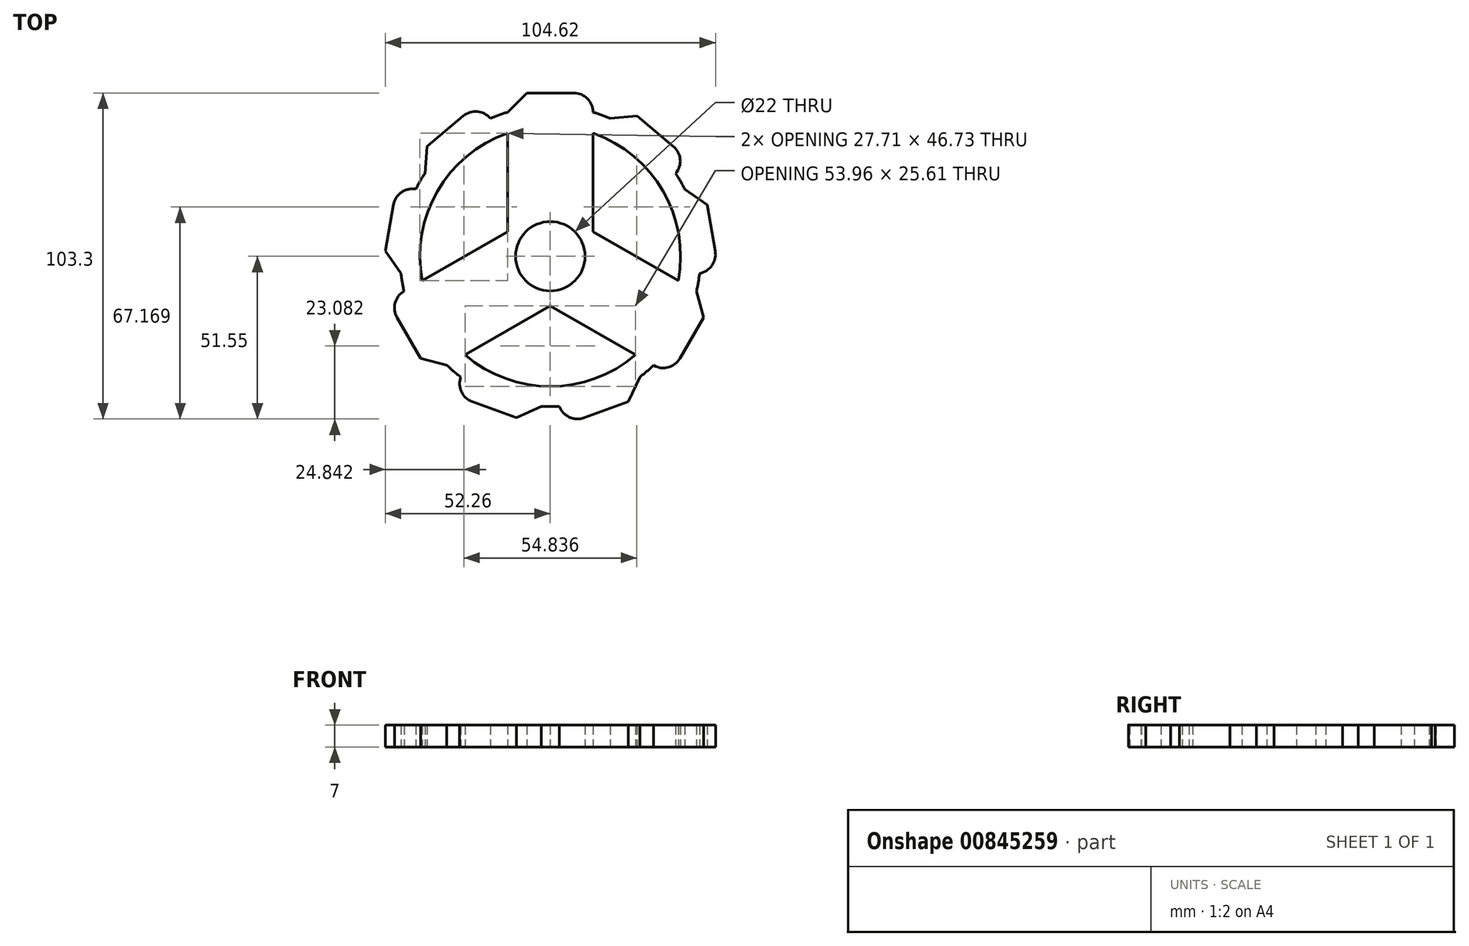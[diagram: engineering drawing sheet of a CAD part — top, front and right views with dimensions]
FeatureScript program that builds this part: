
annotation { "Feature Type Name" : "Feature", "Feature Type Description" : "" }
export const myFeature = defineFeature(function(context is Context, id is Id, definition is map)
    precondition{}
    {
        {
            var Q0;
            Q0=qCreatedBy(makeId("Top.planeOp"),FACE);
            var sketch = newSketch(context, id + "F0", { "sketchPlane" : qUnion([Q0])});
            skCircle(sketch, "E0", {"center": v(0, 0) * mm, "radius": 11 * mm});
            skCircle(sketch, "E1", {"center": v(0, 0) * mm, "radius": 13.56 * mm});
            skArc(sketch, "E2", {"start": v(-13.56, 38.98) * mm, "mid": v(0, -41.28) * mm, "end": v(13.56, 38.98) * mm});
            skArc(sketch, "E3", {"start": v(-13.56, 45.65) * mm, "mid": v(-16.29, 44.75) * mm, "end": v(-18.95, 43.7) * mm});
            skLineSegment(sketch, "E4.left", {"start": v(-13.56, 7.83) * mm, "end": v(-13.56, 38.98) * mm});
            skLineSegment(sketch, "E4.right", {"start": v(13.56, 7.83) * mm, "end": v(13.56, 38.98) * mm});
            skPoint(sketch, "E5.orphan", {"position": v(-13.56, 0) * mm});
            skLineSegment(sketch, "E6.top", {"start": v(-7.46, 51.75) * mm, "end": v(7.46, 51.75) * mm});
            skLineSegment(sketch, "E6.left", {"start": v(-13.56, 38.98) * mm, "end": v(-13.56, 45.65) * mm, "construction": true});
            skLineSegment(sketch, "E6.right", {"start": v(13.56, 38.98) * mm, "end": v(13.56, 45.65) * mm, "construction": true});
            skArc(sketch, "E7.filletArc", {"start": v(13.56, 45.65) * mm, "mid": v(11.78, 49.97) * mm, "end": v(7.46, 51.75) * mm});
            skLineSegment(sketch, "E8", {"start": v(-13.56, 45.65) * mm, "end": v(-7.46, 51.75) * mm});
            skLineSegment(sketch, "E9.1.0", {"start": v(-41.09, -32.34) * mm, "end": v(-48.55, -19.41) * mm});
            skLineSegment(sketch, "E9.1.1", {"start": v(-32.75, -34.57) * mm, "end": v(-41.09, -32.34) * mm});
            skLineSegment(sketch, "E9.1.2", {"start": v(-26.98, -31.24) * mm, "end": v(-32.75, -34.57) * mm, "construction": true});
            skLineSegment(sketch, "E9.1.3", {"start": v(0, -15.66) * mm, "end": v(-26.98, -31.24) * mm});
            skLineSegment(sketch, "E9.1.4", {"start": v(-13.56, 7.83) * mm, "end": v(-40.54, -7.74) * mm});
            skLineSegment(sketch, "E9.1.5", {"start": v(-40.54, -7.74) * mm, "end": v(-46.32, -11.08) * mm, "construction": true});
            skArc(sketch, "E9.1.6", {"start": v(-46.32, -11.08) * mm, "mid": v(-49.16, -14.78) * mm, "end": v(-48.55, -19.41) * mm});
            skLineSegment(sketch, "E9.2.0", {"start": v(48.55, -19.41) * mm, "end": v(41.09, -32.34) * mm});
            skLineSegment(sketch, "E9.2.1", {"start": v(46.32, -11.08) * mm, "end": v(48.55, -19.41) * mm});
            skLineSegment(sketch, "E9.2.2", {"start": v(40.54, -7.74) * mm, "end": v(46.32, -11.08) * mm, "construction": true});
            skLineSegment(sketch, "E9.2.3", {"start": v(13.56, 7.83) * mm, "end": v(40.54, -7.74) * mm});
            skLineSegment(sketch, "E9.2.4", {"start": v(0, -15.66) * mm, "end": v(26.98, -31.24) * mm});
            skLineSegment(sketch, "E9.2.5", {"start": v(26.98, -31.24) * mm, "end": v(32.75, -34.57) * mm, "construction": true});
            skArc(sketch, "E9.2.6", {"start": v(32.75, -34.57) * mm, "mid": v(37.38, -35.18) * mm, "end": v(41.09, -32.34) * mm});
            skPoint(sketch, "E10.orphan", {"position": v(-6.78, 11.75) * mm});
            skPoint(sketch, "E11.orphan", {"position": v(6.78, 11.75) * mm});
            skPoint(sketch, "E12.orphan", {"position": v(13.56, 0) * mm});
            skPoint(sketch, "E13.orphan", {"position": v(6.78, -11.75) * mm});
            skPoint(sketch, "E14.orphan", {"position": v(-6.78, -11.75) * mm});
            skLineSegment(sketch, "E15.1.0", {"start": v(-39.74, 26.25) * mm, "end": v(-38.98, 34.85) * mm});
            skLineSegment(sketch, "E15.1.1", {"start": v(-38.98, 34.85) * mm, "end": v(-27.55, 44.44) * mm});
            skArc(sketch, "E15.1.2", {"start": v(-18.95, 43.7) * mm, "mid": v(-23.1, 45.85) * mm, "end": v(-27.55, 44.44) * mm});
            skLineSegment(sketch, "E15.2.0", {"start": v(-47.31, -5.43) * mm, "end": v(-52.26, 1.64) * mm});
            skLineSegment(sketch, "E15.2.1", {"start": v(-52.26, 1.64) * mm, "end": v(-49.67, 16.34) * mm});
            skArc(sketch, "E15.2.2", {"start": v(-42.6, 21.29) * mm, "mid": v(-47.16, 20.27) * mm, "end": v(-49.67, 16.34) * mm});
            skLineSegment(sketch, "E15.4.0", {"start": v(-2.87, -47.54) * mm, "end": v(-10.69, -51.18) * mm});
            skLineSegment(sketch, "E15.4.1", {"start": v(-10.69, -51.18) * mm, "end": v(-24.71, -46.08) * mm});
            skArc(sketch, "E15.4.2", {"start": v(-28.36, -38.26) * mm, "mid": v(-28.16, -42.92) * mm, "end": v(-24.71, -46.08) * mm});
            skLineSegment(sketch, "E15.5.0", {"start": v(28.36, -38.26) * mm, "end": v(24.71, -46.08) * mm});
            skLineSegment(sketch, "E15.5.1", {"start": v(24.71, -46.08) * mm, "end": v(10.69, -51.18) * mm});
            skArc(sketch, "E15.5.2", {"start": v(2.87, -47.54) * mm, "mid": v(6.02, -50.98) * mm, "end": v(10.69, -51.18) * mm});
            skLineSegment(sketch, "E15.7.0", {"start": v(42.6, 21.29) * mm, "end": v(49.67, 16.34) * mm});
            skLineSegment(sketch, "E15.7.1", {"start": v(49.67, 16.34) * mm, "end": v(52.26, 1.64) * mm});
            skArc(sketch, "E15.7.2", {"start": v(47.31, -5.43) * mm, "mid": v(51.25, -2.92) * mm, "end": v(52.26, 1.64) * mm});
            skLineSegment(sketch, "E15.8.0", {"start": v(18.95, 43.7) * mm, "end": v(27.55, 44.44) * mm});
            skLineSegment(sketch, "E15.8.1", {"start": v(27.55, 44.44) * mm, "end": v(38.98, 34.85) * mm});
            skArc(sketch, "E15.8.2", {"start": v(39.74, 26.25) * mm, "mid": v(41.14, 30.7) * mm, "end": v(38.98, 34.85) * mm});
            skArc(sketch, "E16.trimOffspring", {"start": v(-39.74, 26.25) * mm, "mid": v(-41.24, 23.81) * mm, "end": v(-42.6, 21.29) * mm});
            skArc(sketch, "E17.trimOffspring", {"start": v(-47.31, -5.43) * mm, "mid": v(-46.9, -8.27) * mm, "end": v(-46.32, -11.08) * mm});
            skArc(sketch, "E18.trimOffspring", {"start": v(-32.75, -34.57) * mm, "mid": v(-30.61, -36.48) * mm, "end": v(-28.36, -38.26) * mm});
            skArc(sketch, "E19.trimOffspring", {"start": v(-2.87, -47.54) * mm, "mid": v(0, -47.63) * mm, "end": v(2.87, -47.54) * mm});
            skArc(sketch, "E20.trimOffspring", {"start": v(28.36, -38.26) * mm, "mid": v(30.61, -36.48) * mm, "end": v(32.75, -34.57) * mm});
            skArc(sketch, "E21.trimOffspring", {"start": v(46.32, -11.08) * mm, "mid": v(46.9, -8.27) * mm, "end": v(47.31, -5.43) * mm});
            skArc(sketch, "E22.trimOffspring", {"start": v(42.6, 21.29) * mm, "mid": v(41.24, 23.81) * mm, "end": v(39.74, 26.25) * mm});
            skArc(sketch, "E23.trimOffspring", {"start": v(18.95, 43.7) * mm, "mid": v(16.29, 44.75) * mm, "end": v(13.56, 45.65) * mm});
            skSolve(sketch);
        }
        {
            var Q0;
            Q0=qSketchRegion(id+"F0",true);
            var Q1;
            Q1=makeQuery(id+"F0.imprint","IMPRINT",FACE,{"disambiguationData":[TD([[makeQuery(id+"F0.imprint","IMPRINT",EDGE,{"derivedFrom":sQuery(id+"F0.wireOp",EDGE,"E0")}),-1.0]])]});
            var Q2;
            {var subQ0=sQuery(id+"F0.wireOp",EDGE,"E6.bottom");Q2=makeQuery(id+"F0.imprint","IMPRINT",FACE,{"disambiguationData":[TD([[makeQuery(id+"F0.imprint","IMPRINT",EDGE,{"derivedFrom":subQ0}),1.0]])]});}
            var Q3;
            {var subQ0=sQuery(id+"F0.wireOp",EDGE,"4da5e357-2c40-4844-ab1d-fab356adb77c.3.1");Q3=makeQuery(id+"F0.imprint","IMPRINT",FACE,{"disambiguationData":[TD([[makeQuery(id+"F0.imprint","IMPRINT",EDGE,{"derivedFrom":subQ0}),1.0]])]});}
            var Q4;
            {var subQ0=sQuery(id+"F0.wireOp",EDGE,"4da5e357-2c40-4844-ab1d-fab356adb77c.6.1");Q4=makeQuery(id+"F0.imprint","IMPRINT",FACE,{"disambiguationData":[TD([[makeQuery(id+"F0.imprint","IMPRINT",EDGE,{"derivedFrom":subQ0}),1.0]])]});}
            var Q5;
            Q5=makeQuery(id+"F0.imprint","IMPRINT",FACE,{"disambiguationData":[TD([[makeQuery(id+"F0.imprint","IMPRINT",EDGE,{"derivedFrom":sQuery(id+"F0.wireOp",EDGE,"E1")}),-1.0]])]});
            extrude(context, id + "F1", {"entities" : qUnion([Q0, Q1, Q2, Q3, Q4, Q5]), "depth" : 7 * mm, "offsetDistance" : 25.4 * mm});
        }
    });
